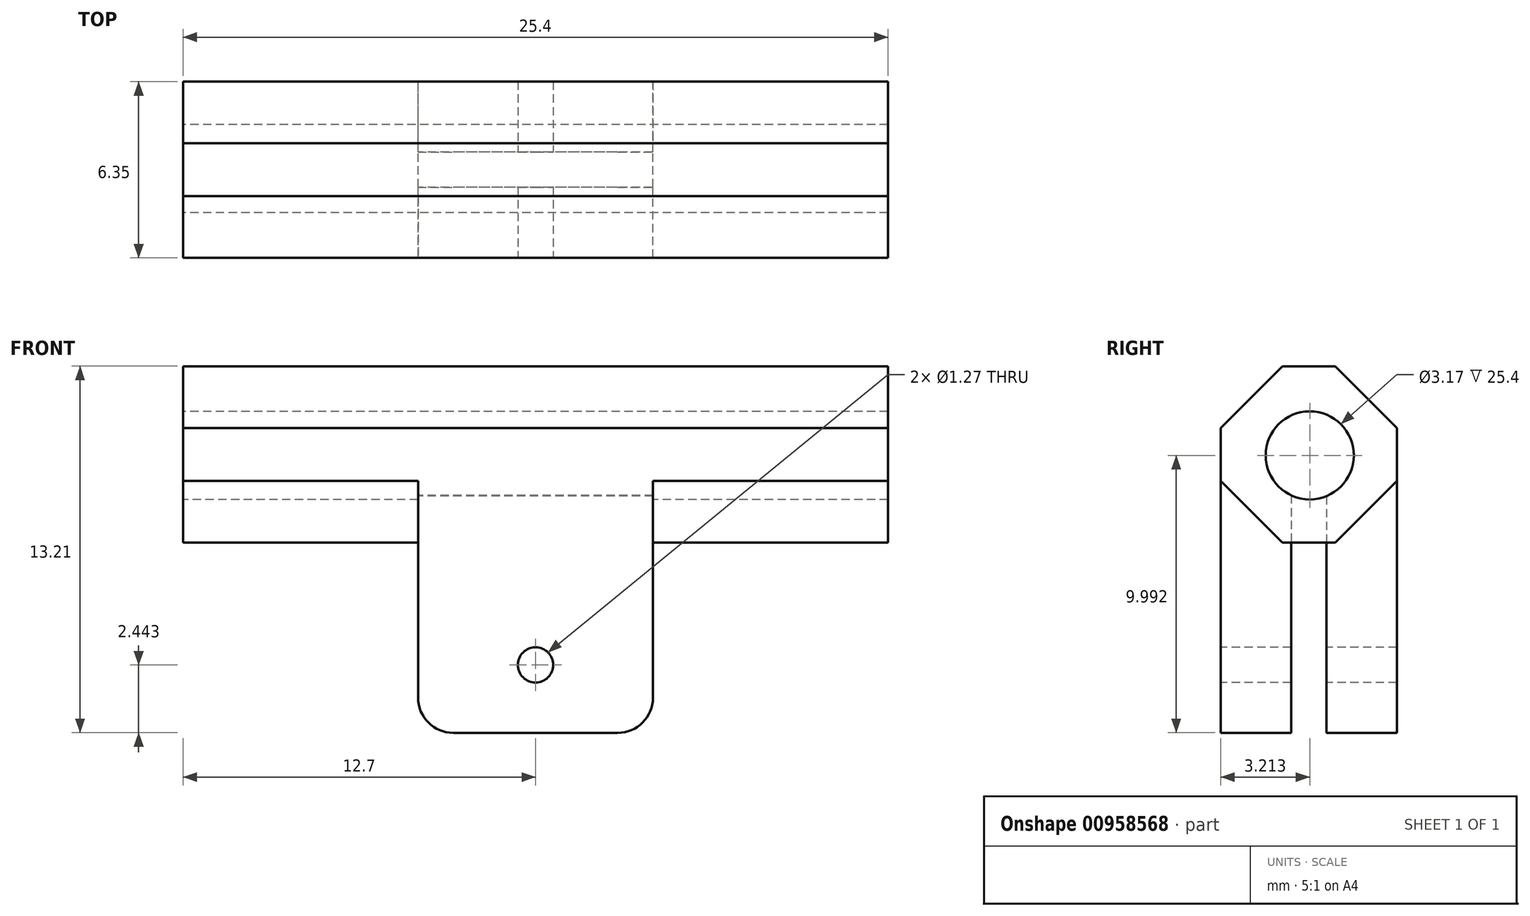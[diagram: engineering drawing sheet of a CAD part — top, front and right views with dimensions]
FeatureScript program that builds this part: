
annotation { "Feature Type Name" : "Feature", "Feature Type Description" : "" }
export const myFeature = defineFeature(function(context is Context, id is Id, definition is map)
    precondition{}
    {
        {
            var Q0;
            Q0=qCreatedBy(makeId("Front.planeOp"),FACE);
            var sketch = newSketch(context, id + "F0", { "sketchPlane" : qUnion([Q0])});
            skLineSegment(sketch, "E0.bottom", {"start": v(12.7, 3.17) * mm, "end": v(-12.7, 3.17) * mm});
            skLineSegment(sketch, "E0.top", {"start": v(12.7, -3.18) * mm, "end": v(-12.7, -3.18) * mm});
            skLineSegment(sketch, "E0.left", {"start": v(12.7, 3.17) * mm, "end": v(12.7, -3.18) * mm});
            skLineSegment(sketch, "E0.right", {"start": v(-12.7, 3.17) * mm, "end": v(-12.7, -3.18) * mm});
            skPoint(sketch, "E0.middle", {"position": v(0, 0) * mm});
            skLineSegment(sketch, "E1.bottom", {"start": v(4.23, -3.18) * mm, "end": v(-4.23, -3.18) * mm});
            skLineSegment(sketch, "E1.top", {"start": v(4.23, -10.03) * mm, "end": v(-4.23, -10.03) * mm});
            skLineSegment(sketch, "E1.left", {"start": v(4.23, -3.18) * mm, "end": v(4.23, -10.03) * mm});
            skLineSegment(sketch, "E1.right", {"start": v(-4.23, -3.18) * mm, "end": v(-4.23, -10.03) * mm});
            skSolve(sketch);
        }
        {
            var Q0;
            Q0=makeQuery(id+"F0.imprint","IMPRINT",FACE,{"disambiguationData":[TD([[makeQuery(id+"F0.imprint","IMPRINT",EDGE,{"derivedFrom":sQuery(id+"F0.wireOp",EDGE,"E0.bottom")}),1.0]])]});
            extrude(context, id + "F1", {"entities" : qUnion([Q0]), "depth" : 6.35 * mm, "offsetDistance" : 25.4 * mm});
        }
        {
            var Q0;
            Q0=makeQuery(id+"F0.imprint","IMPRINT",FACE,{"disambiguationData":[TD([[makeQuery(id+"F0.imprint","IMPRINT",EDGE,{"derivedFrom":sQuery(id+"F0.wireOp",EDGE,"E1.top")}),-1.0]])]});
            extrude(context, id + "F2", {"entities" : qUnion([Q0]), "operationType" : NewBodyOperationType.ADD, "depth" : 6.35 * mm, "offsetDistance" : 25.4 * mm});
        }
        {
            var Q0;
            Q0=makeQuery(id+"F1.opExtrude","CAP_EDGE",EDGE,{"disambiguationData":[OSD([sQuery(id+"F0.wireOp",EDGE,"E0.bottom")])],"isStart":false});
            var Q1;
            {var subQ0=sQuery(id+"F0.wireOp",EDGE,"E0.right");var subQ3=sQuery(id+"F0.wireOp",EDGE,"E0.top");var subQ6=sQuery(id+"F0.wireOp",EDGE,"E0.left");var subQ8=makeQuery(id+"F1.opExtrude","CAP_EDGE",EDGE,{"disambiguationData":[OSD([subQ3])],"isStart":false});Q1=qUnion([makeQuery(id+"F2.boolean.opBoolean","SPLIT",EDGE,{"disambiguationData":[TD([makeQuery(id+"F1.opExtrude","SWEPT_FACE",FACE,{"disambiguationData":[OSD([subQ6])]})])],"derivedFrom":subQ8}),makeQuery(id+"F2.boolean.opBoolean","SPLIT",EDGE,{"disambiguationData":[TD([makeQuery(id+"F1.opExtrude","SWEPT_FACE",FACE,{"disambiguationData":[OSD([subQ0])]})])],"derivedFrom":subQ8})]);}
            var Q2;
            Q2=makeQuery(id+"F1.opExtrude","CAP_EDGE",EDGE,{"disambiguationData":[OSD([sQuery(id+"F0.wireOp",EDGE,"E0.bottom")])],"isStart":true});
            var Q3;
            {var subQ2=sQuery(id+"F0.wireOp",EDGE,"E0.top");var subQ4=sQuery(id+"F0.wireOp",EDGE,"E0.right");var subQ6=sQuery(id+"F0.wireOp",EDGE,"E0.left");var subQ8=makeQuery(id+"F1.opExtrude","CAP_EDGE",EDGE,{"disambiguationData":[OSD([subQ2])],"isStart":true});Q3=qUnion([makeQuery(id+"F2.boolean.opBoolean","SPLIT",EDGE,{"disambiguationData":[TD([makeQuery(id+"F1.opExtrude","SWEPT_FACE",FACE,{"disambiguationData":[OSD([subQ6])]})])],"derivedFrom":subQ8}),makeQuery(id+"F2.boolean.opBoolean","SPLIT",EDGE,{"disambiguationData":[TD([makeQuery(id+"F1.opExtrude","SWEPT_FACE",FACE,{"disambiguationData":[OSD([subQ4])]})])],"derivedFrom":subQ8})]);}
            chamfer(context, id + "F3", {"entities" : qUnion([Q0, Q1, Q2, Q3]), "width" : 2.22 * mm, "tangentPropagation" : true});
        }
        {
            var Q0;
            Q0=makeQuery(id+"F2.opExtrude","SWEPT_EDGE",EDGE,{"disambiguationData":[OSD([sQuery(id+"F0.wireOp",EDGE,"E1.top"),sQuery(id+"F0.wireOp",EDGE,"E1.right")])]});
            var Q1;
            Q1=makeQuery(id+"F2.opExtrude","SWEPT_EDGE",EDGE,{"disambiguationData":[OSD([sQuery(id+"F0.wireOp",EDGE,"E1.top"),sQuery(id+"F0.wireOp",EDGE,"E1.left")])]});
            fillet(context, id + "F4", {"entities" : qUnion([Q0, Q1]), "radius" : 1.27 * mm, "tangentPropagation" : true, "allowEdgeOverflow" : false});
        }
        {
            var Q0;
            Q0=makeQuery(id+"F2.opExtrude","SWEPT_FACE",FACE,{"disambiguationData":[OSD([sQuery(id+"F0.wireOp",EDGE,"E1.top")])]});
            var Q1;
            Q1=makeQuery(id+"F4.opFillet","BLEND_FACE",FACE,{"disambiguationData":[OSD([sQuery(id+"F0.wireOp",EDGE,"E1.top"),sQuery(id+"F0.wireOp",EDGE,"E1.left")])]});
            var Q2;
            Q2=makeQuery(id+"F4.opFillet","BLEND_FACE",FACE,{"disambiguationData":[OSD([sQuery(id+"F0.wireOp",EDGE,"E1.top"),sQuery(id+"F0.wireOp",EDGE,"E1.right")])]});
            var Q3;
            Q3=makeQuery(id+"F2.opExtrude","SWEPT_FACE",FACE,{"disambiguationData":[OSD([sQuery(id+"F0.wireOp",EDGE,"E1.left")])]});
            var Q4;
            Q4=makeQuery(id+"F2.opExtrude","SWEPT_FACE",FACE,{"disambiguationData":[OSD([sQuery(id+"F0.wireOp",EDGE,"E1.right")])]});
            shell(context, id + "F5", {"entities" : qUnion([Q0, Q1, Q2, Q3, Q4]), "thickness" : 2.54 * mm});
        }
        {
            var Q0;
            Q0=makeQuery(id+"F1.opExtrude","SWEPT_FACE",FACE,{"disambiguationData":[OSD([sQuery(id+"F0.wireOp",EDGE,"E0.right")])]});
            var sketch = newSketch(context, id + "F6", { "sketchPlane" : qUnion([Q0])});
            skPoint(sketch, "E2", {"position": v(3.14, -0.04) * mm});
            skSolve(sketch);
        }
        {
            var Q0;
            Q0=sQuery(id+"F6.wireOp",VERTEX,"E2");
            var Q1;
            Q1=makeQuery(id+"F1.opExtrude","SWEPT_BODY",BODY,{"disambiguationData":[OSD([sQuery(id+"F0.wireOp",EDGE,"E0.bottom"),sQuery(id+"F0.wireOp",EDGE,"E0.top"),sQuery(id+"F0.wireOp",EDGE,"E0.left"),sQuery(id+"F0.wireOp",EDGE,"E0.right")])]});
            hole(context, id + "F7", {"style" : HoleStyle.SIMPLE, "endStyle" : HoleEndStyle.BLIND, "holeDiameter" : 3.17 * mm, "majorDiameter" : 6.35 * mm, "holeDepth" : 25.4 * mm, "isTappedThrough" : true, "tappedDepth" : 12.7 * mm, "tapClearance" : 3, "startFromSketch" : true, "locations" : qUnion([Q0]), "scope" : qUnion([Q1])});
        }
        {
            var Q0;
            {var subQ0=sQuery(id+"F0.wireOp",EDGE,"E0.top");Q0=makeQuery(id+"F2.boolean.opBoolean","MERGE",FACE,{"derivedFrom":[makeQuery(id+"F1.opExtrude","CAP_FACE",FACE,{"disambiguationData":[OSD([sQuery(id+"F0.wireOp",EDGE,"E0.bottom"),subQ0,sQuery(id+"F0.wireOp",EDGE,"E0.left"),sQuery(id+"F0.wireOp",EDGE,"E0.right")])],"isStart":false}),makeQuery(id+"F2.opExtrude","CAP_FACE",FACE,{"disambiguationData":[OSD([subQ0,sQuery(id+"F0.wireOp",EDGE,"E1.top"),sQuery(id+"F0.wireOp",EDGE,"E1.left"),sQuery(id+"F0.wireOp",EDGE,"E1.right")])],"isStart":false})]});}
            var sketch = newSketch(context, id + "F8", { "sketchPlane" : qUnion([Q0])});
            skPoint(sketch, "E3", {"position": v(0, -7.59) * mm});
            skPoint(sketch, "E3.positionSnap0", {"position": v(-4.23, -4.86) * mm});
            skSolve(sketch);
        }
        {
            var Q0;
            Q0=sQuery(id+"F8.wireOp",VERTEX,"E3");
            var Q1;
            Q1=makeQuery(id+"F1.opExtrude","SWEPT_BODY",BODY,{"disambiguationData":[OSD([sQuery(id+"F0.wireOp",EDGE,"E0.bottom"),sQuery(id+"F0.wireOp",EDGE,"E0.top"),sQuery(id+"F0.wireOp",EDGE,"E0.left"),sQuery(id+"F0.wireOp",EDGE,"E0.right")])]});
            hole(context, id + "F9", {"style" : HoleStyle.SIMPLE, "endStyle" : HoleEndStyle.BLIND, "holeDiameter" : 1.27 * mm, "majorDiameter" : 6.35 * mm, "holeDepth" : 25.4 * mm, "isTappedThrough" : true, "tappedDepth" : 12.7 * mm, "tapClearance" : 3, "startFromSketch" : true, "locations" : qUnion([Q0]), "scope" : qUnion([Q1])});
        }
    });
